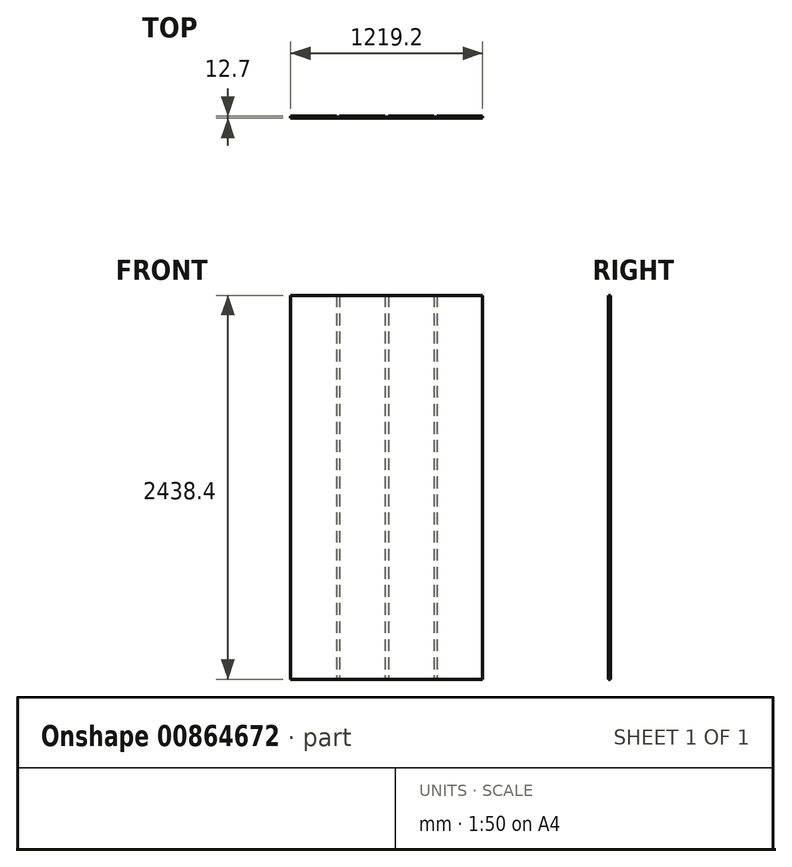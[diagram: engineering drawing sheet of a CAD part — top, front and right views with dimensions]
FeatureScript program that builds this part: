
annotation { "Feature Type Name" : "Feature", "Feature Type Description" : "" }
export const myFeature = defineFeature(function(context is Context, id is Id, definition is map)
    precondition{}
    {
        {
            var Q0;
            Q0=qCreatedBy(makeId("Top.planeOp"),FACE);
            var sketch = newSketch(context, id + "F0", { "sketchPlane" : qUnion([Q0])});
            skLineSegment(sketch, "E0", {"start": v(0, 0) * mm, "end": v(1219.2, 0) * mm});
            skLineSegment(sketch, "E1", {"start": v(1219.2, 0) * mm, "end": v(1219.2, 12.7) * mm});
            skLineSegment(sketch, "E2", {"start": v(0, 12.7) * mm, "end": v(0, 0) * mm});
            skLineSegment(sketch, "E3", {"start": v(289.54, 12.7) * mm, "end": v(289.54, 7.55) * mm});
            skLineSegment(sketch, "E4", {"start": v(289.54, 7.55) * mm, "end": v(309.89, 7.55) * mm});
            skLineSegment(sketch, "E5", {"start": v(309.89, 7.55) * mm, "end": v(309.89, 12.7) * mm});
            skLineSegment(sketch, "E6", {"start": v(309.89, 12.7) * mm, "end": v(599.43, 12.7) * mm});
            skLineSegment(sketch, "E7", {"start": v(599.43, 12.7) * mm, "end": v(599.43, 7.55) * mm});
            skLineSegment(sketch, "E8", {"start": v(599.43, 7.55) * mm, "end": v(619.77, 7.55) * mm});
            skLineSegment(sketch, "E9", {"start": v(619.77, 7.55) * mm, "end": v(619.77, 12.7) * mm});
            skLineSegment(sketch, "E10", {"start": v(619.77, 12.7) * mm, "end": v(909.31, 12.7) * mm});
            skLineSegment(sketch, "E11", {"start": v(909.31, 12.7) * mm, "end": v(909.31, 7.55) * mm});
            skLineSegment(sketch, "E12", {"start": v(909.31, 7.55) * mm, "end": v(929.66, 7.55) * mm});
            skLineSegment(sketch, "E13", {"start": v(929.66, 7.55) * mm, "end": v(929.66, 12.7) * mm});
            skLineSegment(sketch, "E14", {"start": v(929.66, 12.7) * mm, "end": v(1219.2, 12.7) * mm});
            skLineSegment(sketch, "E15", {"start": v(289.54, 12.7) * mm, "end": v(0, 12.7) * mm});
            skSolve(sketch);
        }
        {
            var Q0;
            Q0 = qSketchRegion(id + "F0", true);
            extrude(context, id + "F1", {"entities" : qUnion([Q0]), "depth" : 2438.4 * mm, "offsetDistance" : 25.4 * mm});
        }
    });
